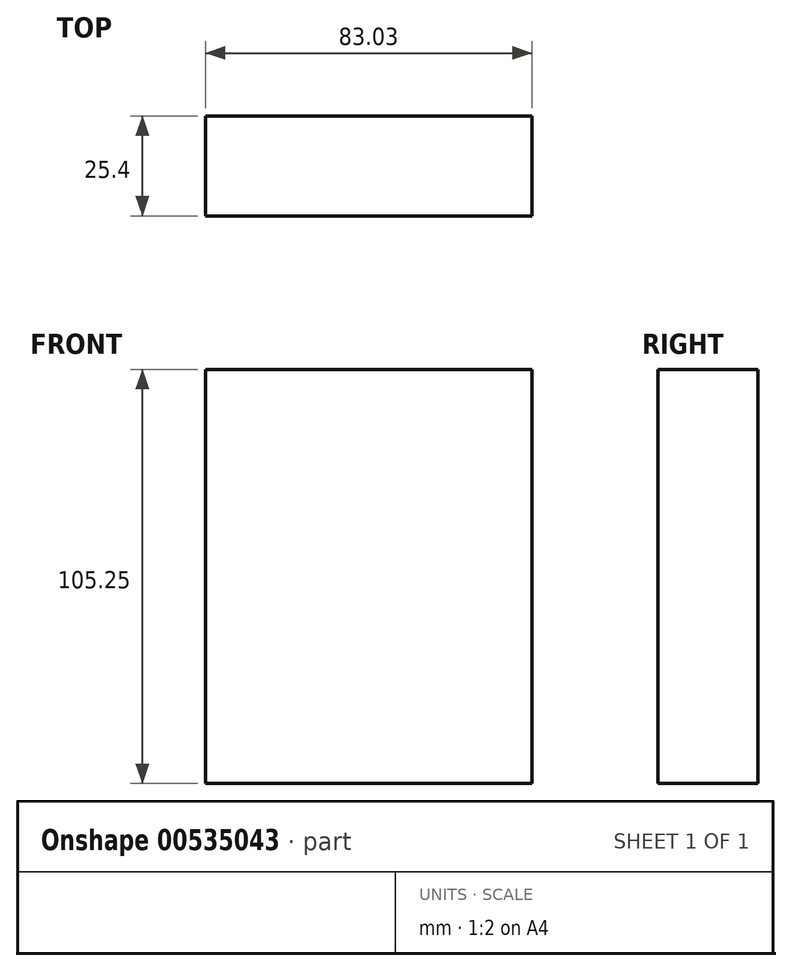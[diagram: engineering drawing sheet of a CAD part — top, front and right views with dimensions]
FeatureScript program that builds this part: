
annotation { "Feature Type Name" : "Feature", "Feature Type Description" : "" }
export const myFeature = defineFeature(function(context is Context, id is Id, definition is map)
    precondition{}
    {
        {
            var Q0;
            Q0=qCreatedBy(makeId("Front.planeOp"),FACE);
            var sketch = newSketch(context, id + "F0", { "sketchPlane" : qUnion([Q0])});
            skLineSegment(sketch, "E0.bottom", {"start": v(-43.66, 61.3) * mm, "end": v(39.37, 61.3) * mm});
            skLineSegment(sketch, "E0.top", {"start": v(-43.66, -43.95) * mm, "end": v(39.37, -43.95) * mm});
            skLineSegment(sketch, "E0.left", {"start": v(-43.66, 61.3) * mm, "end": v(-43.66, -43.95) * mm});
            skLineSegment(sketch, "E0.right", {"start": v(39.37, 61.3) * mm, "end": v(39.37, -43.95) * mm});
            skSolve(sketch);
        }
        {
            var Q0;
            Q0 = qSketchRegion(id + "F0", true);
            extrude(context, id + "F1", {"entities" : qUnion([Q0]), "depth" : 25.4 * mm, "offsetDistance" : 25.4 * mm});
        }
    });
